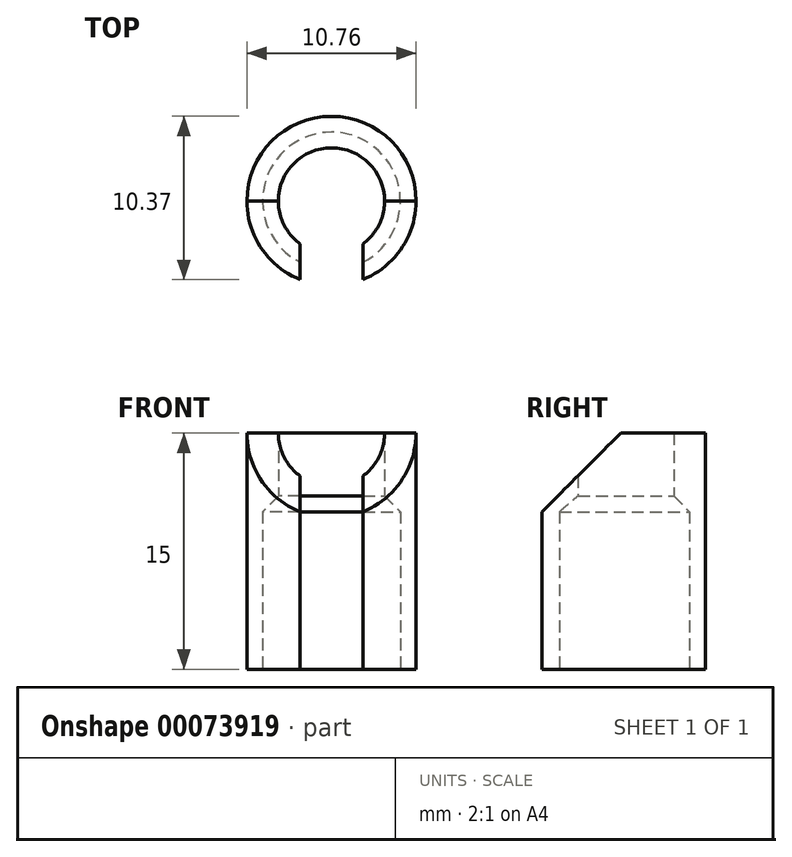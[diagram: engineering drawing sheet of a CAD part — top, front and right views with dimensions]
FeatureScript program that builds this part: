
annotation { "Feature Type Name" : "Feature", "Feature Type Description" : "" }
export const myFeature = defineFeature(function(context is Context, id is Id, definition is map)
    precondition{}
    {
        {
            var Q0;
            Q0=qCreatedBy(makeId("Top.planeOp"),FACE);
            var sketch = newSketch(context, id + "F0", { "sketchPlane" : qUnion([Q0])});
            skArc(sketch, "E0", {"start": v(2, -4.99) * mm, "mid": v(0, 5.38) * mm, "end": v(-2, -4.99) * mm});
            skArc(sketch, "E1", {"start": v(2, -3.9) * mm, "mid": v(0, 4.38) * mm, "end": v(-2, -3.9) * mm});
            skLineSegment(sketch, "E2", {"start": v(0, 0) * mm, "end": v(2, 0) * mm, "construction": true});
            skLineSegment(sketch, "E3", {"start": v(2, 0) * mm, "end": v(2, -4.99) * mm, "construction": true});
            skLineSegment(sketch, "E4", {"start": v(0, 0) * mm, "end": v(-2, 0) * mm, "construction": true});
            skLineSegment(sketch, "E5", {"start": v(-2, 0) * mm, "end": v(-2, -4.99) * mm, "construction": true});
            skLineSegment(sketch, "E6", {"start": v(-2, -3.9) * mm, "end": v(-2, -4.99) * mm});
            skLineSegment(sketch, "E7", {"start": v(2, -3.9) * mm, "end": v(2, -4.99) * mm});
            skSolve(sketch);
        }
        {
            var Q0;
            Q0 = qSketchRegion(id + "F0", true);
            extrude(context, id + "F1", {"entities" : qUnion([Q0]), "depth" : 10 * mm});
        }
        {
            var Q0;
            Q0=makeQuery(id+"F1.opExtrude","CAP_FACE",FACE,{"disambiguationData":[OSD([sQuery(id+"F0.wireOp",EDGE,"E0"),sQuery(id+"F0.wireOp",EDGE,"E1"),sQuery(id+"F0.wireOp",EDGE,"E6"),sQuery(id+"F0.wireOp",EDGE,"E7")])],"isStart":false});
            var sketch = newSketch(context, id + "F2", { "sketchPlane" : qUnion([Q0])});
            skArc(sketch, "E8.0", {"start": v(2, -4.99) * mm, "mid": v(0, 5.38) * mm, "end": v(-2, -4.99) * mm});
            skArc(sketch, "E9", {"start": v(2, -2.72) * mm, "mid": v(0, 3.38) * mm, "end": v(-2, -2.72) * mm});
            skLineSegment(sketch, "E10", {"start": v(-2, -4.99) * mm, "end": v(-2, -2.72) * mm});
            skLineSegment(sketch, "E11", {"start": v(2, -2.72) * mm, "end": v(2, -4.99) * mm});
            skSolve(sketch);
        }
        {
            var Q0;
            Q0 = qSketchRegion(id + "F2", true);
            extrude(context, id + "F3", {"entities" : qUnion([Q0]), "operationType" : NewBodyOperationType.ADD, "depth" : 5 * mm});
        }
        {
            var Q0;
            Q0=makeQuery(id+"F3.opExtrude","CAP_EDGE",EDGE,{"disambiguationData":[OSD([sQuery(id+"F2.wireOp",EDGE,"E9")])],"isStart":true});
            chamfer(context, id + "F4", {"entities" : qUnion([Q0]), "width" : 1 * mm, "tangentPropagation" : true});
        }
        {
            var Q0;
            Q0=qCreatedBy(makeId("Right.planeOp"),FACE);
            var sketch = newSketch(context, id + "F5", { "sketchPlane" : qUnion([Q0])});
            skLineSegment(sketch, "E12.1", {"start": v(-4.99, 15) * mm, "end": v(5.38, 15) * mm});
            skLineSegment(sketch, "E13", {"start": v(-4.99, 15) * mm, "end": v(-4.99, 10) * mm});
            skLineSegment(sketch, "E14", {"start": v(-4.99, 10) * mm, "end": v(0, 15) * mm});
            skSolve(sketch);
        }
        {
            var Q0;
            Q0 = qSketchRegion(id + "F5", true);
            extrude(context, id + "F6", {"entities" : qUnion([Q0]), "operationType" : NewBodyOperationType.REMOVE, "oppositeDirection" : true, "depth" : 25 * mm, "hasSecondDirection" : true, "secondDirectionOppositeDirection" : false, "secondDirectionDepth" : 25 * mm});
        }
    });
